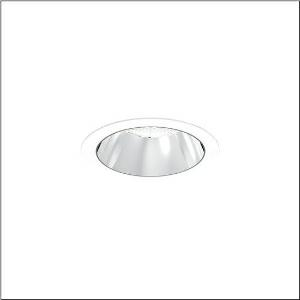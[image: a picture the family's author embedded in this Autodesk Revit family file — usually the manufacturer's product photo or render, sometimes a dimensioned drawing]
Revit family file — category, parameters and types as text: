
# Revit family: lunis_21_l_51db15td91c
name_source: partatom
category: Lighting Fixtures
units: mm (PartAtom-declared; Revit-internal decimal feet)

## family parameters
Cut with Voids When Loaded = No
Host = Face
Light Source = No
Part Type = Normal
Room Calculation Point = No
Round Connector Dimension = Use Diameter
Shared = No

## types (1)
- --- (1 x LED 3000 K ... 6500 K, 4100 lm, 25.4 W, 4000K)
    Apparent Load = 25 VA
    CIE Flux Codes = 93 100 100 100 100
    Color Rendering = 80
    Color Temperature = 4000K
    Default Elevation = 1800 mm
    Description = Lunis 21,  L, downlight, light control with lens, of PMMA, anti glare with reflector, of aluminium, highly specular, light emission: direct distribution, LED rated luminous flux: 4.100lm, light colour: 8tw, with terminal, 5-pole, mains connection: 220..240V, AC/DC, 0/50..60Hz, housing, round, of diecast aluminium, traffic white (RAL 9016), diameter: 165mm, clamping range: 1..40mm, protection rating (complete): IP20, protection rating (on room side): IP54, insulation class (complete): insulation class II (safety insulation), certification: CE, impact resistance: IK03, packaging unit: 1 piece
    Height = 0 mm  [stored 0 ft]
    Lamp = 1 x LED 3000 K ... 6500 K
    Lamp Light Flux = 4100 lm
    Lamp Power = 25.4 W
    Lamp count = 1
    Length = 165 mm
    Luminous efficacy = 161 lm/W
    Manufacturer = Siteco
    ModVariant = No
    Model = 51DB15TD91C
    Mounting Place = Ceiling
    Mounting Type = Recessed
    Number of Poles = 1
    OnlyDefault = Yes
    Power Factor = 1
    Product Name = Lunis 21 L
    Product group = downlight
    ProductGroupID = 400
    Protection Class = Protection class II
    Protection Degree = IP 20
    RLX_Detail_Level = 1
    RLX_Emergency_Light_Flux = 0 lm
    RLX_Emergency_Type = 0
    RLX_Emergency_Type_DB = No
    RlxData = <blob elided: 14809 chars, md5=ba1d6d8a>
    Socket = socket
    Standby Power = 0 W
    System Light Flux = 4100 lm
    System Power = 25 W
    Type Comments = individual setting: CCT=4000K, colour temperature 4000K, luminous flux: 100 % | (ON | ON | OFF | OFF) | 700 mA
    Type Image = l_1291167.jpg
    URL = http://relux.com
    VarID = @adj_020392
    Voltage = 0 V
    Weight = 0.00 kg
    Width = 0 mm  [stored 0 ft]

note: [stored X ft] marks values corroborated as IEEE doubles in the binary element streams (Revit-internal decimal feet)

## geometry (parser evidence)
native form markers: Sweep x11
no freeform markers — native parametric forms only
